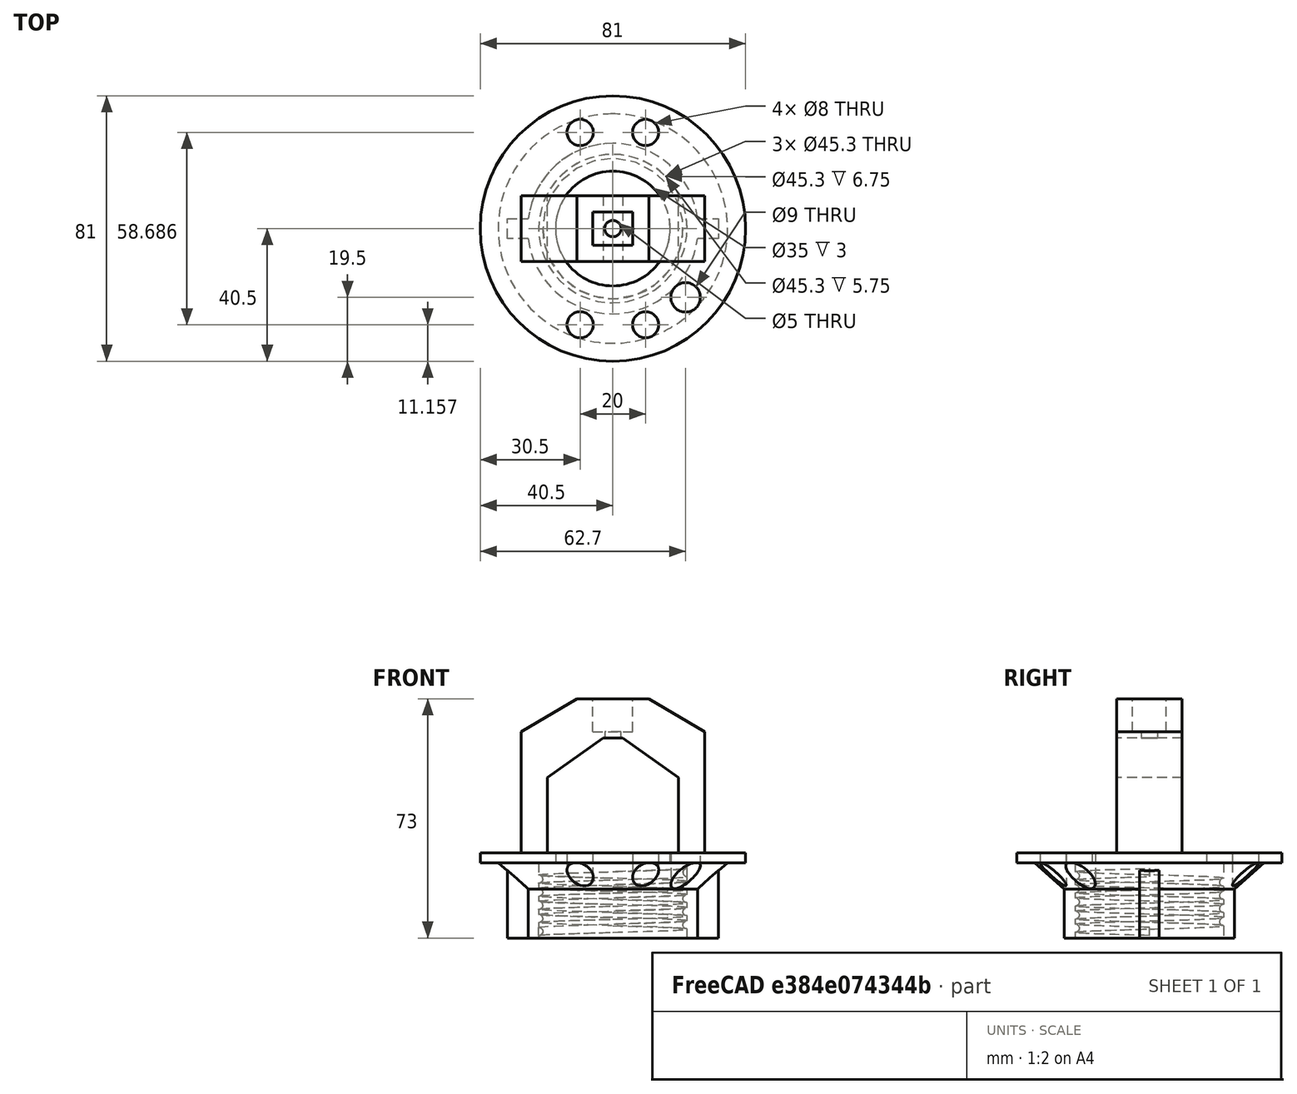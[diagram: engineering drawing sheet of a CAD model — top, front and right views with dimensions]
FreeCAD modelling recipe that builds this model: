
FCSTD DOCUMENT  (FreeCAD 1.0R38641 +678 (Git))
Label: reactor-manifold-GL45
License: All rights reserved
LicenseURL: http://en.wikipedia.org/wiki/All_rights_reserved
objects: Sketcher::SketchObject×9, Part::Extrusion×8, Part::Cut×2, PartDesign::AdditiveHelix×1, PartDesign::Body×1, Part::FeaturePython×1, Part::Revolution×1, Part::MultiCommon×1, Part::MultiFuse×1, Mesh::Feature×1, Part::Cylinder×1
note: 37 computed .brp shape members not serialized (recipe doc carries the construction recipe); baked Part::Feature solids carry a one-line shape summary decoded from their .brp

FEATURE [Sketcher::SketchObject] Sketch
  ArcFitTolerance = 0
  FullyConstrained = true
  MakeInternals = false
  sketch-geometry (9):
    g0: Circle CenterX=0 CenterY=0 CenterZ=0 NormalX=0 NormalY=0 NormalZ=1 AngleXU=0 Radius=22.65
    g1: ArcOfCircle CenterX=0 CenterY=0 CenterZ=0 NormalX=0 NormalY=0 NormalZ=1 AngleXU=0 Radius=26 StartAngle=3.25723 EndAngle=6.16754
    g2: LineSegment StartX=25.8263 StartY=3 StartZ=0 EndX=32.2463 EndY=3 EndZ=0
    g3: LineSegment StartX=32.2463 StartY=3 StartZ=0 EndX=32.2463 EndY=-3 EndZ=0
    g4: LineSegment StartX=32.2463 StartY=-3 StartZ=0 EndX=25.8263 EndY=-3 EndZ=0
    g5: LineSegment StartX=-25.8263 StartY=-3 StartZ=0 EndX=-32.2463 EndY=-3 EndZ=0
    g6: LineSegment StartX=-32.2463 StartY=-3 StartZ=0 EndX=-32.2463 EndY=3 EndZ=0
    g7: LineSegment StartX=-32.2463 StartY=3 StartZ=0 EndX=-25.8263 EndY=3 EndZ=0
    g8: ArcOfCircle CenterX=0 CenterY=0 CenterZ=0 NormalX=0 NormalY=0 NormalZ=1 AngleXU=0 Radius=26 StartAngle=0.115642 EndAngle=3.02595
  constraints (26):
    c: Coincident(g0,g-1)
    c: Diameter(g0) = 45.3  'ThreadOD'
    c: Coincident(g1,g0)
    c: Diameter(g1) = 52  'SleeveOD'
    c: Coincident(g2,g3)
    c: Coincident(g3,g4)
    c: Horizontal(g2)
    c: Horizontal(g4)
    c: Vertical(g3)
    c: Coincident(g5,g6)
    c: Coincident(g6,g7)
    c: Horizontal(g5)
    c: Horizontal(g7)
    c: Vertical(g6)
    c: Equal(g1,g8)
    c: Coincident(g1,g4)
    c: Coincident(g8,g2)
    c: Coincident(g1,g8)
    c: Coincident(g7,g8)
    c: Coincident(g5,g1)
    c: DistanceY(g6,g6) = 6
    c: DistanceY(g3,g3) = 6
    c: DistanceX(g7,g7) = 6.42
    c: DistanceX(g2,g2) = 6.42
    c: Equal(g7,g5)
    c: Equal(g2,g4)
FEATURE [Part::Extrusion] Extrude
  Base = -> Sketch
  Dir = (0,0,1)
  DirMode = 2
  FaceMakerClass = Part::FaceMakerBullseye
  FaceMakerMode = 3
  LengthFwd = 23
  LengthRev = 0
  Solid = true
  Symmetric = false
FEATURE [Sketcher::SketchObject] Sketch001
  ArcFitTolerance = 0
  AttachmentSupport = -> [Extrude]
  FullyConstrained = true
  MakeInternals = false
  MapMode = 5
  Placement = pos=(0,0,23) rot=(0,0,1;0rad)
  expr: Constraints[10] = .Constraints.HeatCoolR
  expr: Constraints[11] = .Constraints.HeatCoolR
  expr: Constraints[12] = .Constraints.HeatCoolR
  sketch-geometry (6):
    g0: Circle CenterX=0 CenterY=0 CenterZ=0 NormalX=0 NormalY=0 NormalZ=1 AngleXU=0 Radius=17.5
    g1: Circle CenterX=0 CenterY=0 CenterZ=0 NormalX=0 NormalY=0 NormalZ=1 AngleXU=0 Radius=40.5
    g2: Circle CenterX=10 CenterY=29.3428 CenterZ=0 NormalX=0 NormalY=0 NormalZ=1 AngleXU=0 Radius=4
    g3: Circle CenterX=-10 CenterY=29.3428 CenterZ=0 NormalX=0 NormalY=0 NormalZ=1 AngleXU=0 Radius=4
    g4: Circle CenterX=10 CenterY=-29.3428 CenterZ=0 NormalX=0 NormalY=0 NormalZ=1 AngleXU=0 Radius=4
    g5: Circle CenterX=-10 CenterY=-29.3428 CenterZ=0 NormalX=0 NormalY=0 NormalZ=1 AngleXU=0 Radius=4
  constraints (16):
    c: Coincident(g0,g-1)
    c: Coincident(g1,g0)
    c: Diameter(g0) = 35
    c: Diameter(g1) = 81
    c: Diameter(g2) = 8  'HeatCoolOD'
    c: Distance(g0,g2) = 31  'HeatCoolR'
    c: DistanceX(g0,g2) = 10  'HeatCoolSep'
    c: Diameter(g3) = 8  'HeatCoolOD'
    c: Diameter(g4) = 8  'HeatCoolOD'
    c: Diameter(g5) = 8  'HeatCoolOD'
    c: Distance(g3,g0) = 31
    c: Distance(g5,g0) = 31
    c: Distance(g4,g0) = 31
    c: DistanceX(g3,g0) = 10
    c: DistanceX(g5,g0) = 10
    c: DistanceX(g0,g4) = 10
FEATURE [Part::Extrusion] Extrude001
  Base = -> Sketch001
  Dir = (0,0,1)
  DirMode = 2
  FaceMakerClass = Part::FaceMakerBullseye
  FaceMakerMode = 3
  LengthFwd = 3
  LengthRev = 0
  Solid = true
  Symmetric = false
FEATURE [Sketcher::SketchObject] Sketch002
  ArcFitTolerance = 0
  AttachmentSupport = -> [Extrude001]
  FullyConstrained = false
  MakeInternals = false
  MapMode = 5
  Placement = pos=(0,0,26) rot=(0,0,1;0rad)
  expr: Constraints[9] = .Constraints.UprightWidth / 2
  sketch-geometry (8):
    g0: LineSegment StartX=20 StartY=10 StartZ=0 EndX=28 EndY=10 EndZ=0
    g1: LineSegment StartX=28 StartY=10 StartZ=0 EndX=28 EndY=-10 EndZ=0
    g2: LineSegment StartX=28 StartY=-10 StartZ=0 EndX=20 EndY=-10 EndZ=0
    g3: LineSegment StartX=20 StartY=-10 StartZ=0 EndX=20 EndY=10 EndZ=0
    g4: LineSegment StartX=-20 StartY=10 StartZ=0 EndX=-28 EndY=10 EndZ=0
    g5: LineSegment StartX=-28 StartY=10 StartZ=0 EndX=-28 EndY=-10 EndZ=0
    g6: LineSegment StartX=-28 StartY=-10 StartZ=0 EndX=-20 EndY=-10 EndZ=0
    g7: LineSegment StartX=-20 StartY=-10 StartZ=0 EndX=-20 EndY=10 EndZ=0
  constraints (20):
    c: Coincident(g0,g1)
    c: Coincident(g1,g2)
    c: Coincident(g2,g3)
    c: Coincident(g3,g0)
    c: Horizontal(g0)
    c: Horizontal(g2)
    c: Vertical(g1)
    c: Vertical(g3)
    c: DistanceY(g3,g3) = 20  'UprightWidth'
    c: DistanceY(g-1,g0) = 10
    c: DistanceX(g0,g0) = 8  'UprightThickness'
    c: DistanceX(g-1,g0) = 20  'UprightRadius'
    c: Coincident(g4,g5)
    c: Coincident(g5,g6)
    c: Coincident(g6,g7)
    c: Coincident(g7,g4)
    c: Horizontal(g4)
    c: Horizontal(g6)
    c: Vertical(g5)
    c: Vertical(g7)
FEATURE [Part::Extrusion] Extrude002
  Base = -> Sketch002
  Dir = (0,0,1)
  DirMode = 2
  FaceMakerClass = Part::FaceMakerBullseye
  FaceMakerMode = 3
  LengthFwd = 35
  LengthRev = 0
  Solid = true
  Symmetric = false
FEATURE [Sketcher::SketchObject] Sketch003
  ArcFitTolerance = 0
  AttachmentSupport = -> [Extrude002]
  FullyConstrained = true
  MakeInternals = false
  MapMode = 5
  Placement = pos=(0,0,61) rot=(0,0,1;0rad)
  expr: .Constraints.PlateWidth = 2 * (Sketch002.Constraints.UprightThickness + Sketch002.Constraints.UprightRadius)
  expr: Constraints[11] = .Constraints.PlateWidth / 2
  expr: Constraints[8] = Sketch002.Constraints.UprightWidth
  expr: Constraints[9] = Sketch002.Constraints.UprightWidth / 2
  sketch-geometry (5):
    g0: LineSegment StartX=-28 StartY=10 StartZ=0 EndX=28 EndY=10 EndZ=0
    g1: LineSegment StartX=28 StartY=10 StartZ=0 EndX=28 EndY=-10 EndZ=0
    g2: LineSegment StartX=28 StartY=-10 StartZ=0 EndX=-28 EndY=-10 EndZ=0
    g3: LineSegment StartX=-28 StartY=-10 StartZ=0 EndX=-28 EndY=10 EndZ=0
    g4: Circle CenterX=0 CenterY=0 CenterZ=0 NormalX=0 NormalY=0 NormalZ=1 AngleXU=0 Radius=2.5
  constraints (14):
    c: Coincident(g0,g1)
    c: Coincident(g1,g2)
    c: Coincident(g2,g3)
    c: Coincident(g3,g0)
    c: Horizontal(g0)
    c: Horizontal(g2)
    c: Vertical(g1)
    c: Vertical(g3)
    c: DistanceY(g3,g3) = 20
    c: DistanceY(g-1,g0) = 10
    c: DistanceX(g0,g0) = 56  'PlateWidth'
    c: DistanceX(g0,g-1) = 28
    c: Coincident(g4,g-1)
    c: Diameter(g4) = 5
FEATURE [Part::Extrusion] Extrude003
  Base = -> Sketch003
  Dir = (0,0,1)
  DirMode = 2
  FaceMakerClass = Part::FaceMakerBullseye
  FaceMakerMode = 3
  LengthFwd = 2
  LengthRev = 0
  Solid = true
  Symmetric = false
FEATURE [Sketcher::SketchObject] Sketch004
  ArcFitTolerance = 0
  AttachmentSupport = -> [Extrude003]
  FullyConstrained = true
  MakeInternals = false
  MapMode = 5
  Placement = pos=(0,0,63) rot=(0,0,1;0rad)
  expr: Constraints[10] = 2 * (Sketch002.Constraints.UprightThickness + Sketch002.Constraints.UprightRadius)
  expr: Constraints[11] = Sketch002.Constraints.UprightThickness + Sketch002.Constraints.UprightRadius
  expr: Constraints[21] = .Constraints.MotorWidth / 2
  expr: Constraints[23] = .Constraints.MotorThickness / 2
  expr: Constraints[8] = Sketch002.Constraints.UprightWidth
  expr: Constraints[9] = Sketch002.Constraints.UprightWidth / 2
  sketch-geometry (8):
    g0: LineSegment StartX=-28 StartY=10 StartZ=0 EndX=28 EndY=10 EndZ=0
    g1: LineSegment StartX=28 StartY=10 StartZ=0 EndX=28 EndY=-10 EndZ=0
    g2: LineSegment StartX=28 StartY=-10 StartZ=0 EndX=-28 EndY=-10 EndZ=0
    g3: LineSegment StartX=-28 StartY=-10 StartZ=0 EndX=-28 EndY=10 EndZ=0
    g4: LineSegment StartX=-6.1 StartY=5.1 StartZ=0 EndX=6.1 EndY=5.1 EndZ=0
    g5: LineSegment StartX=6.1 StartY=5.1 StartZ=0 EndX=6.1 EndY=-5.1 EndZ=0
    g6: LineSegment StartX=6.1 StartY=-5.1 StartZ=0 EndX=-6.1 EndY=-5.1 EndZ=0
    g7: LineSegment StartX=-6.1 StartY=-5.1 StartZ=0 EndX=-6.1 EndY=5.1 EndZ=0
  constraints (24):
    c: Coincident(g0,g1)
    c: Coincident(g1,g2)
    c: Coincident(g2,g3)
    c: Coincident(g3,g0)
    c: Horizontal(g0)
    c: Horizontal(g2)
    c: Vertical(g1)
    c: Vertical(g3)
    c: DistanceY(g3,g3) = 20
    c: DistanceY(g-1,g0) = 10
    c: DistanceX(g0,g0) = 56
    c: DistanceX(g-1,g0) = 28
    c: Coincident(g4,g5)
    c: Coincident(g5,g6)
    c: Coincident(g6,g7)
    c: Coincident(g7,g4)
    c: Horizontal(g4)
    c: Horizontal(g6)
    c: Vertical(g5)
    c: Vertical(g7)
    c: DistanceX(g4,g4) = 12.2  'MotorWidth'
    c: DistanceX(g-1,g4) = 6.1
    c: DistanceY(g5,g5) = 10.2  'MotorThickness'
    c: DistanceY(g-1,g4) = 5.1
FEATURE [Part::Extrusion] Extrude004
  Base = -> Sketch004
  Dir = (0,0,1)
  DirMode = 2
  FaceMakerClass = Part::FaceMakerBullseye
  FaceMakerMode = 3
  LengthFwd = 10
  LengthRev = 0
  Solid = true
  Symmetric = false
FEATURE [Sketcher::SketchObject] Sketch005
  ArcFitTolerance = 0
  FullyConstrained = true
  MakeInternals = false
  Placement = pos=(0,0,0) rot=(1,0,0;1.5708rad)
  expr: Constraints[1] = Sketch.Constraints.ThreadOD / 2
  expr: Constraints[4] = Sketch.Constraints.ThreadOD / 2
  sketch-geometry (2):
    g0: ArcOfCircle CenterX=-22.65 CenterY=2 CenterZ=0 NormalX=0 NormalY=0 NormalZ=1 AngleXU=0 Radius=1.25 StartAngle=4.71239 EndAngle=7.85398
    g1: LineSegment StartX=-22.65 StartY=0.75 StartZ=0 EndX=-22.65 EndY=3.25 EndZ=0
  constraints (7):
    c: Diameter(g0) = 2.5  'ThreadD'
    c: DistanceX(g0,g-1) = 22.65
    c: DistanceY(g-1,g0) = 2  'ThreadStartH'
    c: Vertical(g1)
    c: DistanceX(g1,g-1) = 22.65
    c: Coincident(g0,g1)
    c: Coincident(g0,g1)
FEATURE [PartDesign::AdditiveHelix] AdditiveHelix
  Angle = 0
  Axis = (0,2e-16,1)
  Base = (0,0,0)
  Growth = 0
  HasBeenEdited = true
  Height = 18
  LeftHanded = false
  Mode = 0
  Outside = false
  Pitch = 4
  Placement = pos=(0,0,0) rot=(1,0,0;1.5708rad)
  Profile = -> Sketch005
  ReferenceAxis = -> Sketch005 [V_Axis]
  Suppressed = false
  Tolerance = 0.1
  Turns = 4.5
FEATURE [PartDesign::Body] Body
  AllowCompound = false
  Group = -> [Sketch005,AdditiveHelix]
  Origin = -> Origin
  Tip = -> AdditiveHelix
FEATURE [Part::FeaturePython] Connect  # WARN: FeaturePython — macro-defined, semantics opaque (R4)
  Objects = -> [Extrude003,Extrude002]
  Tolerance = 0
FEATURE [Sketcher::SketchObject] Sketch006
  ArcFitTolerance = 0
  FullyConstrained = true
  MakeInternals = false
  Placement = pos=(0,0,0) rot=(1,0,0;1.5708rad)
  expr: Constraints[5] = Sketch002.Constraints.UprightRadius
  sketch-geometry (6):
    g0: LineSegment StartX=-20 StartY=49 StartZ=0 EndX=-3 EndY=61 EndZ=0
    g1: LineSegment StartX=-20 StartY=49 StartZ=0 EndX=-20 EndY=61 EndZ=0
    g2: LineSegment StartX=-20 StartY=61 StartZ=0 EndX=-3 EndY=61 EndZ=0
    g3: LineSegment StartX=20 StartY=49 StartZ=0 EndX=3 EndY=61 EndZ=0
    g4: LineSegment StartX=20 StartY=49 StartZ=0 EndX=20 EndY=61 EndZ=0
    g5: LineSegment StartX=20 StartY=61 StartZ=0 EndX=3 EndY=61 EndZ=0
  constraints (18):
    c: Coincident(g1,g0)
    c: Vertical(g1)
    c: Coincident(g2,g1)
    c: Coincident(g2,g0)
    c: Horizontal(g2)
    c: DistanceX(g0,g-1) = 20
    c: DistanceX(g0,g-1) = 3
    c: DistanceY(g-1,g0) = 61  'H'
    c: DistanceY(g-1,g0) = 49
    c: Coincident(g4,g3)
    c: Vertical(g4)
    c: Coincident(g5,g4)
    c: Coincident(g5,g3)
    c: Horizontal(g5)
    c: DistanceY(g-1,g3) = 61
    c: DistanceY(g-1,g3) = 49
    c: DistanceX(g-1,g3) = 3
    c: DistanceX(g-1,g3) = 20
FEATURE [Part::Extrusion] Extrude005
  Base = -> Sketch006
  Dir = (0,-1,2e-16)
  DirMode = 2
  FaceMakerClass = Part::FaceMakerBullseye
  FaceMakerMode = 3
  LengthFwd = 20
  LengthRev = 0
  Solid = true
  Symmetric = true
FEATURE [Sketcher::SketchObject] Sketch007
  ArcFitTolerance = 0
  FullyConstrained = true
  MakeInternals = false
  Placement = pos=(0,0,0) rot=(0.57735,0.57735,0.57735;2.0944rad)
  expr: Constraints[3] = Sketch.Constraints.SleeveOD / 2
  sketch-geometry (3):
    g0: LineSegment StartX=26 StartY=23 StartZ=0 EndX=26 EndY=15 EndZ=0
    g1: LineSegment StartX=26 StartY=15 StartZ=0 EndX=35 EndY=23 EndZ=0
    g2: LineSegment StartX=35 StartY=23 StartZ=0 EndX=26 EndY=23 EndZ=0
  constraints (9):
    c: Vertical(g0)
    c: Coincident(g1,g0)
    c: Horizontal(g2)
    c: DistanceX(g-1,g0) = 26
    c: DistanceX(g-1,g1) = 35
    c: Coincident(g2,g1)
    c: DistanceY(g-1,g2) = 23
    c: DistanceY(g-1,g0) = 15
    c: Coincident(g0,g2)
FEATURE [Part::Revolution] Revolve
  Angle = 360
  Axis = (0,0,1)
  Base = (0,0,0)
  FaceMakerClass = Part::FaceMakerBullseye
  Solid = true
  Source = -> Sketch007
  Symmetric = false
FEATURE [Part::Extrusion] Extrude007
  Base = -> Sketch001
  Dir = (0,0,1)
  DirMode = 2
  FaceMakerClass = Part::FaceMakerBullseye
  FaceMakerMode = 3
  LengthFwd = 0
  LengthRev = 15
  Solid = true
  Symmetric = false
FEATURE [Part::MultiCommon] Common
  Shapes = -> [Revolve,Extrude007]
FEATURE [Sketcher::SketchObject] Sketch008
  ArcFitTolerance = 0
  AttachmentSupport = -> [Extrude004]
  FullyConstrained = true
  MakeInternals = false
  MapMode = 5
  Placement = pos=(0,10,0) rot=(0,0.707107,0.707107;3.14159rad)
  sketch-geometry (6):
    g0: LineSegment StartX=-28 StartY=63 StartZ=0 EndX=-11 EndY=73 EndZ=0
    g1: LineSegment StartX=-11 StartY=73 StartZ=0 EndX=-28 EndY=73 EndZ=0
    g2: LineSegment StartX=-28 StartY=73 StartZ=0 EndX=-28 EndY=63 EndZ=0
    g3: LineSegment StartX=28 StartY=63 StartZ=0 EndX=11 EndY=73 EndZ=0
    g4: LineSegment StartX=11 StartY=73 StartZ=0 EndX=28 EndY=73 EndZ=0
    g5: LineSegment StartX=28 StartY=73 StartZ=0 EndX=28 EndY=63 EndZ=0
  constraints (18):
    c: Coincident(g0,g1)
    c: Horizontal(g1)
    c: Coincident(g1,g2)
    c: Coincident(g2,g0)
    c: Vertical(g2)
    c: DistanceY(g-1,g0) = 63
    c: DistanceY(g-1,g1) = 73
    c: DistanceX(g0,g-1) = 28
    c: DistanceX(g0,g-1) = 11
    c: Coincident(g3,g4)
    c: Horizontal(g4)
    c: Coincident(g4,g5)
    c: Coincident(g5,g3)
    c: Vertical(g5)
    c: DistanceY(g-1,g3) = 63
    c: DistanceY(g-1,g4) = 73
    c: DistanceX(g-1,g3) = 28
    c: DistanceX(g-1,g3) = 11
FEATURE [Part::Extrusion] Extrude008
  Base = -> Sketch008
  Dir = (0,1,-2e-16)
  DirMode = 2
  FaceMakerClass = Part::FaceMakerBullseye
  FaceMakerMode = 3
  LengthFwd = 0
  LengthRev = 20
  Solid = true
  Symmetric = false
FEATURE [Part::Cut] Cut
  Base = -> Extrude004
  Tool = -> Extrude008
FEATURE [Part::MultiFuse] Fusion
  Shapes = -> [Cut,Extrude,Extrude001,Body,Connect,Extrude005,Common]
FEATURE [Mesh::Feature] Mesh  label="Fusion (Meshed)"
FEATURE [Part::Cylinder] Cylinder
  Angle = 360
  AttacherType = Attacher::AttachEngine3D
  FirstAngle = 0
  Height = 20
  Placement = pos=(22.2,-21,13.8) rot=(0,0,1;0rad)
  Radius = 4.5
  SecondAngle = 0
FEATURE [Part::Cut] Cut001
  Base = -> Fusion
  Tool = -> Cylinder
